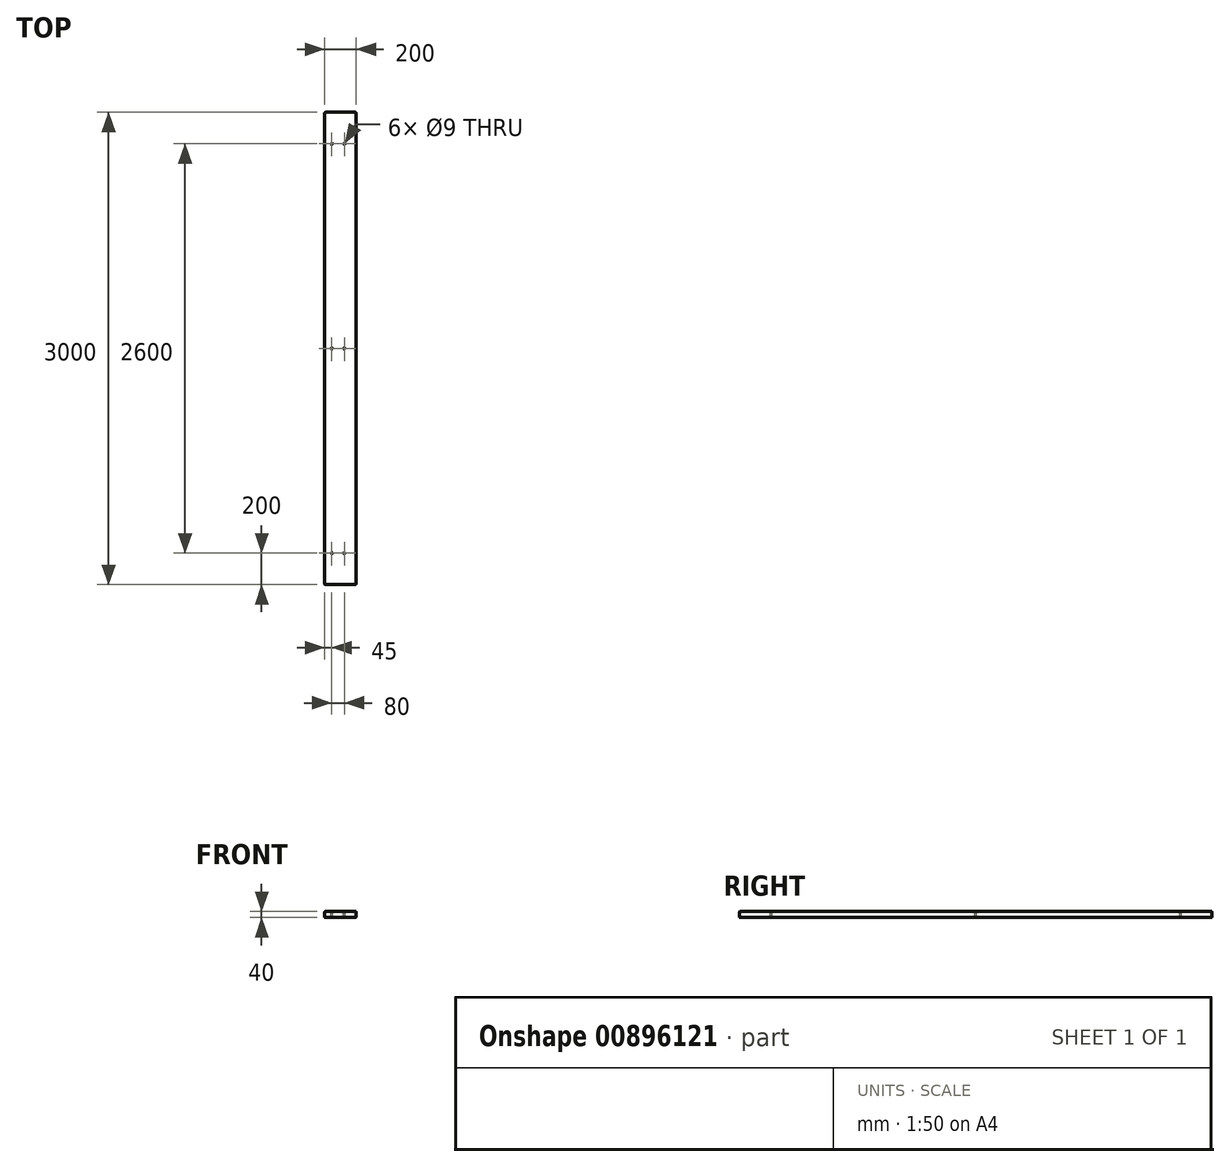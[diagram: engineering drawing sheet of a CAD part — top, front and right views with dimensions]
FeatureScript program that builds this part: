
annotation { "Feature Type Name" : "Feature", "Feature Type Description" : "" }
export const myFeature = defineFeature(function(context is Context, id is Id, definition is map)
    precondition{}
    {
        {
            var Q0;
            Q0=qCreatedBy(makeId("Front.planeOp"),FACE);
            var sketch = newSketch(context, id + "F0", { "sketchPlane" : qUnion([Q0])});
            skLineSegment(sketch, "E0.bottom", {"start": v(0, 0) * mm, "end": v(200, 0) * mm});
            skLineSegment(sketch, "E0.top", {"start": v(0, 40) * mm, "end": v(200, 40) * mm});
            skLineSegment(sketch, "E0.left", {"start": v(0, 0) * mm, "end": v(0, 40) * mm});
            skLineSegment(sketch, "E0.right", {"start": v(200, 0) * mm, "end": v(200, 40) * mm});
            skSolve(sketch);
        }
        {
            var Q0;
            Q0=qSketchRegion(id+"F0",true);
            extrude(context, id + "F1", {"entities" : qUnion([Q0]), "depth" : 3000 * mm, "offsetDistance" : 25 * mm});
        }
        {
            var Q0;
            Q0=makeQuery(id+"F1.opExtrude","SWEPT_FACE",FACE,{"disambiguationData":[OSD([sQuery(id+"F0.wireOp",EDGE,"E0.top")])]});
            var sketch = newSketch(context, id + "F2", { "sketchPlane" : qUnion([Q0])});
            skLineSegment(sketch, "E1", {"start": v(0, -3000) * mm, "end": v(45, -3000) * mm, "construction": true});
            skLineSegment(sketch, "E2", {"start": v(45, -3000) * mm, "end": v(125, -3000) * mm, "construction": true});
            skLineSegment(sketch, "E3", {"start": v(45, -3000) * mm, "end": v(45, -2800) * mm, "construction": true});
            skLineSegment(sketch, "E4", {"start": v(45, -2800) * mm, "end": v(45, -200) * mm, "construction": true});
            skLineSegment(sketch, "E5", {"start": v(45, -200) * mm, "end": v(45, 0) * mm, "construction": true});
            skLineSegment(sketch, "E6", {"start": v(125, -3000) * mm, "end": v(125, -2800) * mm, "construction": true});
            skLineSegment(sketch, "E7", {"start": v(125, -2800) * mm, "end": v(125, -200) * mm, "construction": true});
            skLineSegment(sketch, "E8", {"start": v(125, -200) * mm, "end": v(125, 0) * mm, "construction": true});
            skCircle(sketch, "E9", {"center": v(45, -2800) * mm, "radius": 4.5 * mm});
            skCircle(sketch, "E10", {"center": v(125, -2800) * mm, "radius": 4.5 * mm});
            skCircle(sketch, "E11", {"center": v(45, -200) * mm, "radius": 4.5 * mm});
            skCircle(sketch, "E12", {"center": v(125, -200) * mm, "radius": 4.5 * mm});
            skPoint(sketch, "E13", {"position": v(45, -1500) * mm});
            skPoint(sketch, "E14", {"position": v(125, -1500) * mm});
            skCircle(sketch, "E15", {"center": v(45, -1500) * mm, "radius": 4.5 * mm});
            skCircle(sketch, "E16", {"center": v(125, -1500) * mm, "radius": 4.5 * mm});
            skSolve(sketch);
        }
        {
            var Q0;
            Q0=qSketchRegion(id+"F2",true);
            extrude(context, id + "F3", {"entities" : qUnion([Q0]), "operationType" : NewBodyOperationType.REMOVE, "endBound" : BoundingType.THROUGH_ALL, "oppositeDirection" : true, "depth" : 25 * mm, "offsetDistance" : 25 * mm});
        }
        {
            var Q0;
            Q0=makeQuery(id+"F1.opExtrude","SWEPT_EDGE",EDGE,{"disambiguationData":[OSD([sQuery(id+"F0.wireOp",EDGE,"E0.top"),sQuery(id+"F0.wireOp",EDGE,"E0.left")])]});
            var Q1;
            Q1=makeQuery(id+"F1.opExtrude","SWEPT_EDGE",EDGE,{"disambiguationData":[OSD([sQuery(id+"F0.wireOp",EDGE,"E0.bottom"),sQuery(id+"F0.wireOp",EDGE,"E0.left")])]});
            var Q2;
            Q2=makeQuery(id+"F1.opExtrude","SWEPT_EDGE",EDGE,{"disambiguationData":[OSD([sQuery(id+"F0.wireOp",EDGE,"E0.top"),sQuery(id+"F0.wireOp",EDGE,"E0.right")])]});
            var Q3;
            Q3=makeQuery(id+"F1.opExtrude","SWEPT_EDGE",EDGE,{"disambiguationData":[OSD([sQuery(id+"F0.wireOp",EDGE,"E0.bottom"),sQuery(id+"F0.wireOp",EDGE,"E0.right")])]});
            var Q4;
            Q4=makeQuery(id+"F1.opExtrude","CAP_EDGE",EDGE,{"disambiguationData":[OSD([sQuery(id+"F0.wireOp",EDGE,"E0.top")])],"isStart":false});
            var Q5;
            Q5=makeQuery(id+"F1.opExtrude","CAP_EDGE",EDGE,{"disambiguationData":[OSD([sQuery(id+"F0.wireOp",EDGE,"E0.bottom")])],"isStart":false});
            var Q6;
            Q6=makeQuery(id+"F1.opExtrude","CAP_EDGE",EDGE,{"disambiguationData":[OSD([sQuery(id+"F0.wireOp",EDGE,"E0.left")])],"isStart":false});
            var Q7;
            Q7=makeQuery(id+"F1.opExtrude","CAP_EDGE",EDGE,{"disambiguationData":[OSD([sQuery(id+"F0.wireOp",EDGE,"E0.right")])],"isStart":false});
            var Q8;
            Q8=makeQuery(id+"F1.opExtrude","CAP_EDGE",EDGE,{"disambiguationData":[OSD([sQuery(id+"F0.wireOp",EDGE,"E0.right")])],"isStart":true});
            var Q9;
            Q9=makeQuery(id+"F1.opExtrude","CAP_EDGE",EDGE,{"disambiguationData":[OSD([sQuery(id+"F0.wireOp",EDGE,"E0.top")])],"isStart":true});
            var Q10;
            Q10=makeQuery(id+"F1.opExtrude","CAP_EDGE",EDGE,{"disambiguationData":[OSD([sQuery(id+"F0.wireOp",EDGE,"E0.bottom")])],"isStart":true});
            var Q11;
            Q11=makeQuery(id+"F1.opExtrude","CAP_EDGE",EDGE,{"disambiguationData":[OSD([sQuery(id+"F0.wireOp",EDGE,"E0.left")])],"isStart":true});
            fillet(context, id + "F4", {"entities" : qUnion([Q0, Q1, Q2, Q3, Q4, Q5, Q6, Q7, Q8, Q9, Q10, Q11]), "radius" : 5 * mm, "tangentPropagation" : true, "allowEdgeOverflow" : false});
        }
    });
